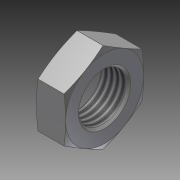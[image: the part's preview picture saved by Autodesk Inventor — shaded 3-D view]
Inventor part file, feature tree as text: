
AUTODESK INVENTOR PART (.ipt)
format: ipt  version: 2014 SP1 (Build 180222100, 222)  size: 109,056 bytes
history: native  units: in
note: dims shown in document units (in); Inventor stores cm internally (conversion verified against a paired STEP export)
features: thread x1, imported_body x1
ambient origin geometry x8: Origin, YZ Plane, XZ Plane, XY Plane, X Axis, Y Axis, Z Axis, Center Point
bodies: Body1 (feature_tree)
feature tree (2):
  thread  "Thread1"  [1 undecoded]
  imported_body  "Base1"
note: 1 required parameter value undecoded (feature->parameter linkage not recoverable at this tier; creation-order binding heuristic only, values carry confidence <= 0.55)
